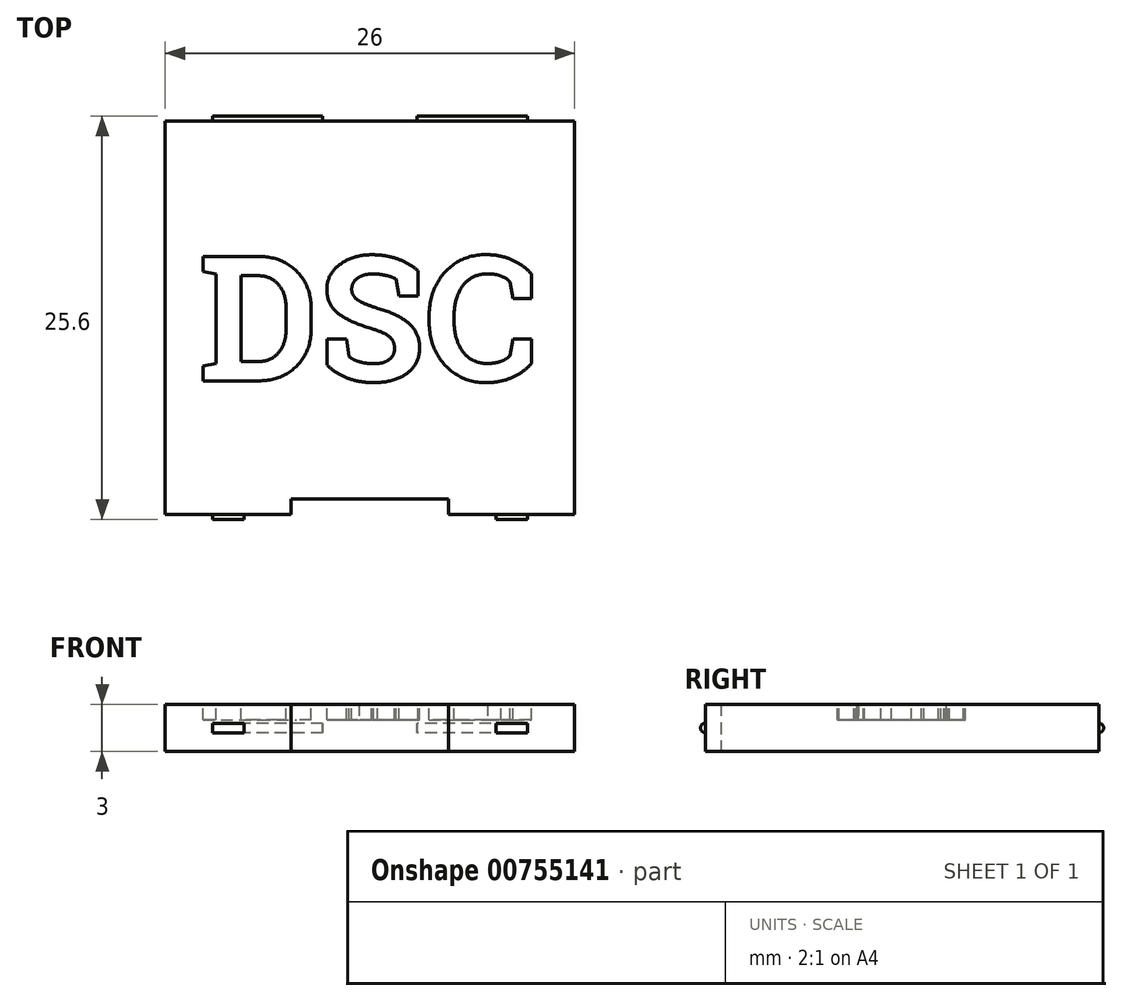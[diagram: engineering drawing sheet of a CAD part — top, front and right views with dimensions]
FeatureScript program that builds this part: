
annotation { "Feature Type Name" : "Feature", "Feature Type Description" : "" }
export const myFeature = defineFeature(function(context is Context, id is Id, definition is map)
    precondition{}
    {
        {
            var Q0;
            Q0=qCreatedBy(makeId("Top.planeOp"),FACE);
            var sketch = newSketch(context, id + "F0", { "sketchPlane" : qUnion([Q0])});
            skLineSegment(sketch, "E0.bottom", {"start": v(-13, 12.5) * mm, "end": v(13, 12.5) * mm});
            skLineSegment(sketch, "E0.top", {"start": v(-13, -12.5) * mm, "end": v(-5, -12.5) * mm});
            skLineSegment(sketch, "E0.left", {"start": v(-13, 12.5) * mm, "end": v(-13, -12.5) * mm});
            skLineSegment(sketch, "E0.right", {"start": v(13, 12.5) * mm, "end": v(13, -12.5) * mm});
            skLineSegment(sketch, "E1.top", {"start": v(-5, -11.5) * mm, "end": v(5, -11.5) * mm});
            skLineSegment(sketch, "E1.left", {"start": v(-5, -12.5) * mm, "end": v(-5, -11.5) * mm});
            skLineSegment(sketch, "E1.right", {"start": v(5, -12.5) * mm, "end": v(5, -11.5) * mm});
            skLineSegment(sketch, "E2.trimOffspring", {"start": v(5, -12.5) * mm, "end": v(13, -12.5) * mm});
            skSolve(sketch);
        }
        {
            var Q0;
            Q0=makeQuery(id+"F0.imprint","IMPRINT",FACE,{"disambiguationData":[TD([[makeQuery(id+"F0.imprint","IMPRINT",EDGE,{"derivedFrom":sQuery(id+"F0.wireOp",EDGE,"E0.bottom")}),-1.0]])]});
            extrude(context, id + "F1", {"entities" : qUnion([Q0]), "depth" : 3 * mm, "offsetDistance" : 25 * mm});
        }
        {
            var Q0;
            Q0=makeQuery(id+"F1.opExtrude","CAP_FACE",FACE,{"disambiguationData":[OSD([sQuery(id+"F0.wireOp",EDGE,"E0.bottom"),sQuery(id+"F0.wireOp",EDGE,"E0.top"),sQuery(id+"F0.wireOp",EDGE,"E0.left"),sQuery(id+"F0.wireOp",EDGE,"E0.right"),sQuery(id+"F0.wireOp",EDGE,"E1.top"),sQuery(id+"F0.wireOp",EDGE,"E1.left"),sQuery(id+"F0.wireOp",EDGE,"E1.right"),sQuery(id+"F0.wireOp",EDGE,"E2.trimOffspring")])],"isStart":false});
            var sketch = newSketch(context, id + "F2", { "sketchPlane" : qUnion([Q0])});
            skText(sketch, "E3", { "text": "DSC", "fontName": "RobotoSlab-Bold.ttf"});
            const initialGuessF2  = {"E3": [-0.01092, -0.004, 1, 0, 0.008]};
            skSetInitialGuess(sketch, initialGuessF2);
            skSolve(sketch);
        }
        {
            var Q0;
            Q0 = qSketchRegion(id + "F2", true);
            extrude(context, id + "F3", {"entities" : qUnion([Q0]), "operationType" : NewBodyOperationType.REMOVE, "oppositeDirection" : true, "depth" : 1 * mm, "offsetDistance" : 25 * mm});
        }
        {
            var Q0;
            Q0=makeQuery(id+"F1.opExtrude","SWEPT_FACE",FACE,{"disambiguationData":[OSD([sQuery(id+"F0.wireOp",EDGE,"E0.left")])]});
            var sketch = newSketch(context, id + "F4", { "sketchPlane" : qUnion([Q0])});
            skArc(sketch, "E4", {"start": v(-12.5, 1.8) * mm, "mid": v(-12.8, 1.5) * mm, "end": v(-12.5, 1.2) * mm});
            skArc(sketch, "E5", {"start": v(12.5, 1.2) * mm, "mid": v(12.8, 1.5) * mm, "end": v(12.5, 1.8) * mm});
            skSolve(sketch);
        }
        {
            var Q0;
            Q0=makeQuery(id+"F1.opExtrude","SWEPT_FACE",FACE,{"disambiguationData":[OSD([sQuery(id+"F0.wireOp",EDGE,"E0.left")])]});
            cPlane(context, id + "F5", {"entities" : qUnion([Q0]), "cplaneType" : CPlaneType.OFFSET, "offset" : 5 * mm, "oppositeDirection" : true, "width" : 150 * mm, "height" : 150 * mm});
        }
        {
            var Q0;
            Q0=qCreatedBy(id+"F5.planeOp",FACE);
            cPlane(context, id + "F6", {"entities" : qUnion([Q0]), "cplaneType" : CPlaneType.OFFSET, "offset" : 5 * mm, "oppositeDirection" : true, "width" : 150 * mm, "height" : 150 * mm});
        }
        {
            var Q0;
            Q0=qCreatedBy(id+"F6.planeOp",FACE);
            cPlane(context, id + "F7", {"entities" : qUnion([Q0]), "cplaneType" : CPlaneType.OFFSET, "offset" : 6 * mm, "oppositeDirection" : true, "width" : 150 * mm, "height" : 150 * mm});
        }
        {
            var Q0;
            Q0=qCreatedBy(id+"F7.planeOp",FACE);
            cPlane(context, id + "F8", {"entities" : qUnion([Q0]), "cplaneType" : CPlaneType.OFFSET, "offset" : 5 * mm, "oppositeDirection" : true, "width" : 150 * mm, "height" : 150 * mm});
        }
        {
            var Q0;
            Q0=qCreatedBy(id+"F5.planeOp",FACE);
            cPlane(context, id + "F9", {"entities" : qUnion([Q0]), "cplaneType" : CPlaneType.OFFSET, "offset" : 2 * mm, "width" : 150 * mm, "height" : 150 * mm});
        }
        {
            var Q0;
            Q0=qCreatedBy(id+"F8.planeOp",FACE);
            cPlane(context, id + "F10", {"entities" : qUnion([Q0]), "cplaneType" : CPlaneType.OFFSET, "offset" : 2 * mm, "oppositeDirection" : true, "width" : 150 * mm, "height" : 150 * mm});
        }
        {
            var Q0;
            {var subQ0=sQuery(id+"F4.wireOp",EDGE,"E4");Q0=makeQuery(id+"F4.imprint","IMPRINT",FACE,{"disambiguationData":[TD([[makeQuery(id+"F4.imprint","IMPRINT",EDGE,{"derivedFrom":subQ0}),1.0]])]});}
            var Q1;
            Q1=sQuery(id+"F4.wireOp",EDGE,"E4");
            var Q2;
            Q2=qCreatedBy(id+"F6.planeOp",FACE);
            var Q3;
            Q3=qCreatedBy(id+"F9.planeOp",FACE);
            extrude(context, id + "F11", {"entities" : qUnion([Q0]), "operationType" : NewBodyOperationType.ADD, "surfaceOperationType" : NewSurfaceOperationType.ADD, "surfaceEntities" : qUnion([Q1]), "endBound" : BoundingType.UP_TO_SURFACE, "oppositeDirection" : true, "depth" : 25 * mm, "endBoundEntityFace" : qUnion([Q2]), "offsetDistance" : 5 * mm, "offsetOppositeDirection" : true, "hasSecondDirection" : true, "secondDirectionBound" : SecondDirectionBoundingType.UP_TO_SURFACE, "secondDirectionOppositeDirection" : true, "secondDirectionDepth" : 25 * mm, "secondDirectionBoundEntityFace" : qUnion([Q3])});
        }
        {
            var Q0;
            {var subQ0=sQuery(id+"F4.wireOp",EDGE,"E4");Q0=makeQuery(id+"F4.imprint","IMPRINT",FACE,{"disambiguationData":[TD([[makeQuery(id+"F4.imprint","IMPRINT",EDGE,{"derivedFrom":subQ0}),1.0]])]});}
            var Q1;
            Q1=qCreatedBy(id+"F10.planeOp",FACE);
            var Q2;
            Q2=qCreatedBy(id+"F7.planeOp",FACE);
            extrude(context, id + "F12", {"entities" : qUnion([Q0]), "operationType" : NewBodyOperationType.ADD, "endBound" : BoundingType.UP_TO_SURFACE, "oppositeDirection" : true, "depth" : 25 * mm, "endBoundEntityFace" : qUnion([Q1]), "offsetDistance" : 25 * mm, "hasSecondDirection" : true, "secondDirectionBound" : SecondDirectionBoundingType.UP_TO_SURFACE, "secondDirectionOppositeDirection" : true, "secondDirectionDepth" : 25 * mm, "secondDirectionBoundEntityFace" : qUnion([Q2])});
        }
        {
            var Q0;
            {var subQ0=sQuery(id+"F4.wireOp",EDGE,"E5");Q0=makeQuery(id+"F4.imprint","IMPRINT",FACE,{"disambiguationData":[TD([[makeQuery(id+"F4.imprint","IMPRINT",EDGE,{"derivedFrom":subQ0}),1.0]])]});}
            var Q1;
            Q1=qCreatedBy(id+"F5.planeOp",FACE);
            var Q2;
            Q2=qCreatedBy(id+"F9.planeOp",FACE);
            extrude(context, id + "F13", {"entities" : qUnion([Q0]), "operationType" : NewBodyOperationType.ADD, "endBound" : BoundingType.UP_TO_SURFACE, "oppositeDirection" : true, "depth" : 25 * mm, "endBoundEntityFace" : qUnion([Q1]), "offsetDistance" : 25 * mm, "hasSecondDirection" : true, "secondDirectionBound" : SecondDirectionBoundingType.UP_TO_SURFACE, "secondDirectionOppositeDirection" : true, "secondDirectionDepth" : 25 * mm, "secondDirectionBoundEntityFace" : qUnion([Q2])});
        }
        {
            var Q0;
            {var subQ0=sQuery(id+"F4.wireOp",EDGE,"E5");Q0=makeQuery(id+"F4.imprint","IMPRINT",FACE,{"disambiguationData":[TD([[makeQuery(id+"F4.imprint","IMPRINT",EDGE,{"derivedFrom":subQ0}),1.0]])]});}
            var Q1;
            Q1=qCreatedBy(id+"F10.planeOp",FACE);
            var Q2;
            Q2=qCreatedBy(id+"F8.planeOp",FACE);
            extrude(context, id + "F14", {"entities" : qUnion([Q0]), "operationType" : NewBodyOperationType.ADD, "endBound" : BoundingType.UP_TO_SURFACE, "oppositeDirection" : true, "depth" : 25 * mm, "endBoundEntityFace" : qUnion([Q1]), "offsetDistance" : 25 * mm, "hasSecondDirection" : true, "secondDirectionBound" : SecondDirectionBoundingType.UP_TO_SURFACE, "secondDirectionOppositeDirection" : true, "secondDirectionDepth" : 25 * mm, "secondDirectionBoundEntityFace" : qUnion([Q2])});
        }
    });
